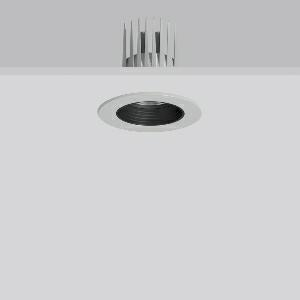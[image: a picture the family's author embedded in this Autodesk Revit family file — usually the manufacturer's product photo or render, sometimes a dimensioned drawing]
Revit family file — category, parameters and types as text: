
# Revit family: heledon_mini_e_901745_004_2_b756
name_source: partatom
category: Lighting Fixtures
units: mm (PartAtom-declared; Revit-internal decimal feet)

## family parameters
Cut with Voids When Loaded = No
Host = Face
Light Source = No
Part Type = Normal
Room Calculation Point = No
Round Connector Dimension = Use Diameter
Shared = No

## types (1)
- HELEDON mini E (1 x LED Modul 927, 1900 lm, 2700)
    Apparent Load = 20 VA
    Approval mark = CE
    CIE Flux Codes = 98 100 100 100 100
    Color Rendering = 92
    Color Temperature = 2700
    Default Elevation = 1800 mm
    Description = Series: HELEDON mini
Round recessed downlight. Housing: die-cast aluminium, powder-coated. Black plastic ring and recessed LED to prevent glare from the side. Optical assembly with lens made of plastic (polycarbonate) for the best homogeneous light distribution - can be changed without tools. Best colour rendering index Ra>90. Suitable for Recessed ceiling mounting. Installation without tools thanks to spring fastening system. Including separate LED converter with connecting cable 600 mm.High quality converter without flickering and stroboscopic effect. Through-wiring box (5 pole) available as accessory. The following accessories can be mounted without use of tools: interchangeable lenses, decorative glasses, honeycomb louvre, clear and frosted diffusers, white interchangeable plastic ring. 
Colour: silver
Diameter: 124 mm
Height: 3 mm
Cut-out diameter: 114 mm
Recess height: 170 mm
Luminaire: recess height: 120 mm
Lamp: LED
Socket: without socket
Colour temperature: 2700K
Colour rendering index (CRI): 92
System power: 20 W
Rated luminous flux: 1900 lm
Luminous efficiency: 95 lm/W
Control gear: Regulated power supply
Protection class: II
Type of protection: IP 20
    Height = 0 mm  [stored 0 ft]
    Lamp = 1 x LED Modul 927
    Lamp Light Flux = 1900 lm
    Lamp count = 1
    Length = 124 mm  [stored 0.406824 ft]
    Lifetime = 50000 h
    Luminous efficacy = 95 lm/W
    Manufacturer = RZB
    ModVariant = No
    Model = 901745.004.2
    Mounting Place = Ceiling
    Mounting Type = Recessed
    Number of Poles = 1
    OnlyDefault = Yes
    Power Factor = 1
    Product Name = HELEDON mini E
    Product group = Recessed downlights
    ProductGroupID = 402
    Protection Class = Protection class II
    Protection Degree = IP 20
    RLX_Detail_Level = 1
    RLX_Emergency_Light_Flux = 0 lm
    RLX_Emergency_Type = 0
    RLX_Emergency_Type_DB = No
    RlxData = <blob elided: 122945 chars, md5=6e1166b9>
    Socket = socket
    Standby Power = 0 W
    System Light Flux = 1900 lm
    System Power = 20 W
    Type Comments = Product without accessories
    Type Image = 901656.004.jpg
    URL = http://relux.com
    VarID = ---
    Voltage = 230 V
    Voltage Range = 220-240 V
    Weight = 0.00 kg
    Width = 0 mm  [stored 0 ft]

note: [stored X ft] marks values corroborated as IEEE doubles in the binary element streams (Revit-internal decimal feet)

## geometry (parser evidence)
native form markers: Blend x4, Sweep x12
no freeform markers — native parametric forms only
